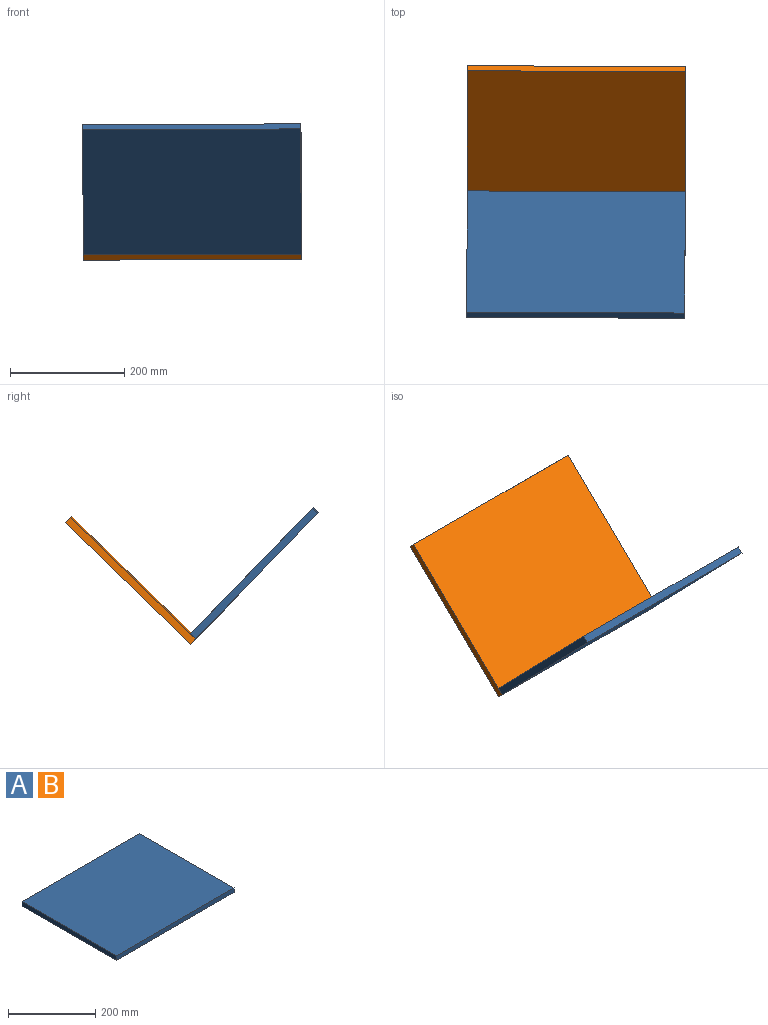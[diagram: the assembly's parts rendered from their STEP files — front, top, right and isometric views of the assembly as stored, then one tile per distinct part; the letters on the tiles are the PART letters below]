
ASSEMBLY  parts=2 mates=1
PART A: 6 faces, bbox 381x304.8x12.7 mm
  f0: plane 381x12.7mm, normal (0,-1,0), area 4838.7mm2, adj f1,f3,f4,f5
  f1: plane 304.8x12.7mm, normal (1,0,0), area 3871mm2, adj f0,f2,f4,f5
  f2: plane 381x12.7mm, normal (0,1,0), area 4838.7mm2, adj f1,f3,f4,f5
  f3: plane 304.8x12.7mm, normal (-1,0,0), area 3871mm2, adj f0,f2,f4,f5
  f4: plane 381x304.8mm, normal (0,0,1), area 116128.8mm2, adj f0,f1,f2,f3
  f5: plane 381x304.8mm, normal (0,0,-1), area 116128.8mm2, adj f0,f1,f2,f3
PART B: same geometry as A
PLACE A rot(axis=(-1,0,-0.01),45.8deg) t=(-109.36,-142.49,-62.81)mm
PLACE B rot(axis=(1,-0.01,0),44.2deg) t=(-108.42,81.86,-75.12)mm
MATE fastened A.f2 <-> B.f4  axis (0.01,0.7,-0.72) through (82,-37.09,-171.38)mm
